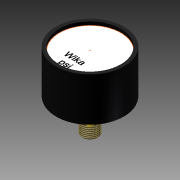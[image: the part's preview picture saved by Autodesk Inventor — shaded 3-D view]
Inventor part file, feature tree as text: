
AUTODESK INVENTOR PART (.ipt)
format: ipt  version: 2011 (Build 150239000, 239)  size: 119,808 bytes
history: native  units: mm (DEFAULTED — no unit token found)
features: sketch x6, extrude x5, thread x1, chamfer x1, fillet x1
ambient origin geometry x8: Origin, YZ Plane, XZ Plane, XY Plane, X Axis, Y Axis, Z Axis, Center Point
bodies: Solid1 (feature_tree)
feature tree (14):
  extrude  "Extrusion13"  Depth=26.0mm TaperAngle=0.0deg
  extrude  "Extrusion15"  Depth=14.0mm
  extrude  "Extrusion16"  Depth=10.0mm TaperAngle=0.0deg
  thread  "Thread3"  [1 undecoded]
  extrude  "Extrusion18"  Depth=2.0mm
  extrude  "Extrusion19"  Depth=0.5mm TaperAngle=45.0deg
  sketch  "Sketch19"  dims[d67=2.0mm d68=0.0mm d69=0.5mm d70=2.0mm d71=45.0deg]
  chamfer  "Chamfer1"  Distance=10.0mm
  fillet  "Fillet5"  Radius=3.0mm
  sketch  "Sketch13"  dims[d46=40.0mm d47=26.0mm d48=0.0mm]
  sketch  "Sketch15"  dims[d52=14.0mm d53=14.0mm]
  sketch  "Sketch16"  dims[d54=8.0mm d55=0.0mm d56=10.0mm d57=0.0mm d58=9.525mm]
  sketch  "Sketch18"  dims[d59=10.0mm d60=0.0mm d66=2.0mm]
  sketch  "Sketch20"  dims[d72=1.0mm d73=10.0mm d74=0.0mm d75=3.0mm]
note: 1 required parameter value undecoded (feature->parameter linkage not recoverable at this tier; creation-order binding heuristic only, values carry confidence <= 0.55)
